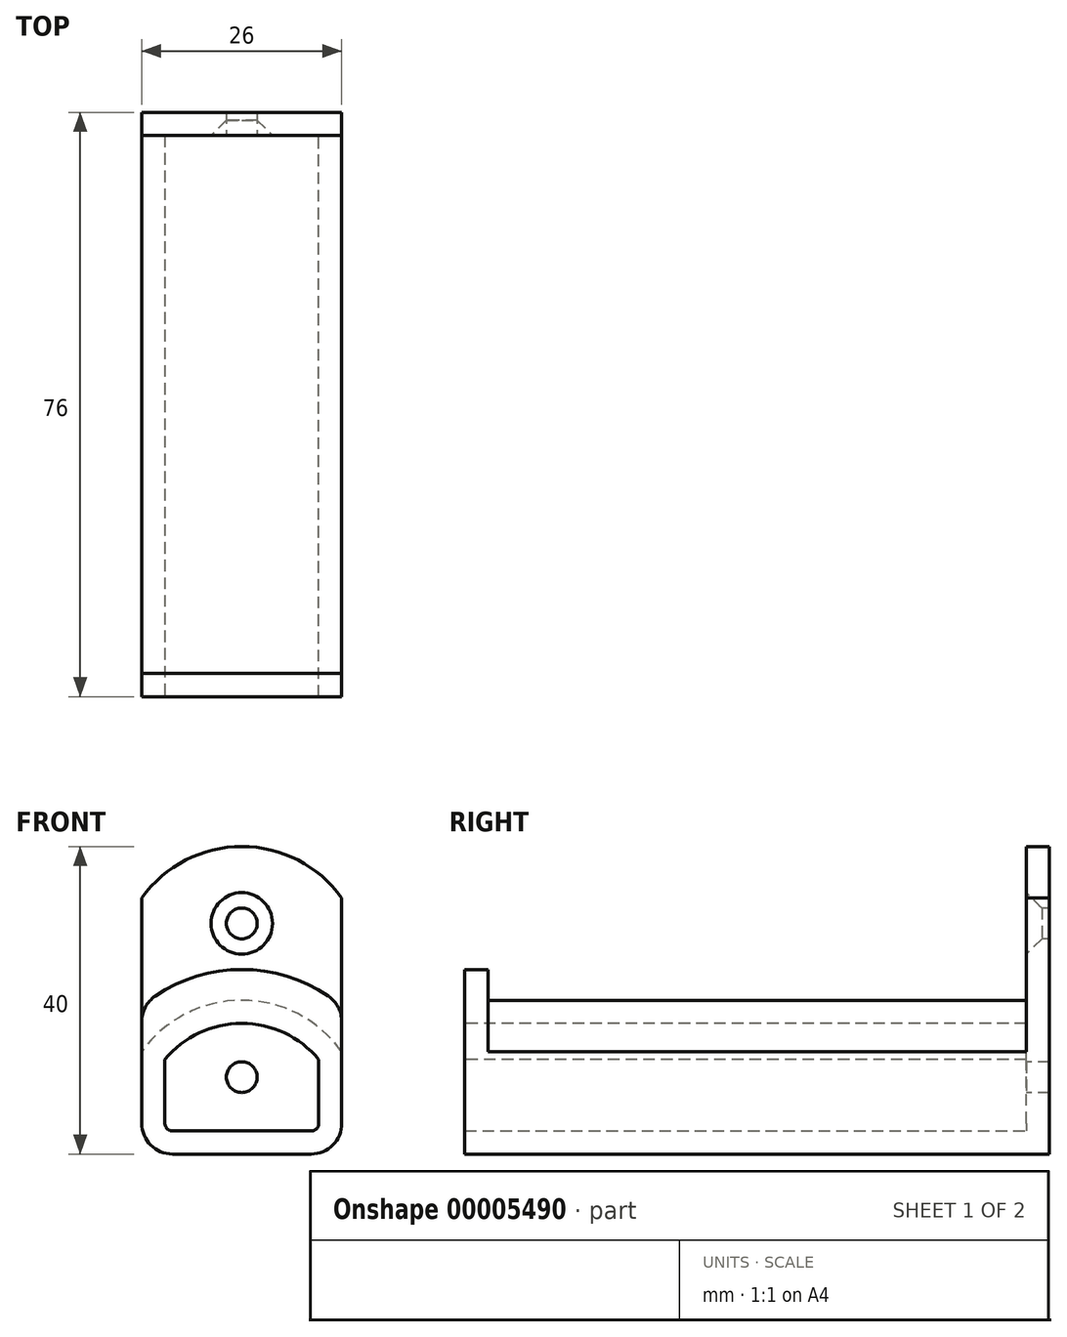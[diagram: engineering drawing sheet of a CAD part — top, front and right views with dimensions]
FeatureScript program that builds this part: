
annotation { "Feature Type Name" : "Feature", "Feature Type Description" : "" }
export const myFeature = defineFeature(function(context is Context, id is Id, definition is map)
    precondition{}
    {
        {
            var Q0;
            Q0=qCreatedBy(makeId("Front.planeOp"),FACE);
            var sketch = newSketch(context, id + "F0", { "sketchPlane" : qUnion([Q0])});
            skArc(sketch, "E0", {"start": v(13, 9.33) * mm, "mid": v(0, 16) * mm, "end": v(-13, 9.33) * mm});
            skLineSegment(sketch, "E1", {"start": v(-13, -4) * mm, "end": v(13, -4) * mm});
            skCircle(sketch, "E2", {"center": v(0, 5.33) * mm, "radius": 16 * mm, "construction": true});
            skLineSegment(sketch, "E3", {"start": v(-13, -4) * mm, "end": v(-13, 9.33) * mm});
            skLineSegment(sketch, "E4", {"start": v(13, -4) * mm, "end": v(13, 9.33) * mm});
            skLineSegment(sketch, "E5", {"start": v(0, 0) * mm, "end": v(0, 24.31) * mm, "construction": true});
            skLineSegment(sketch, "E6", {"start": v(-13, 9.33) * mm, "end": v(-13, 15.2) * mm});
            skLineSegment(sketch, "E7", {"start": v(13, 9.33) * mm, "end": v(13, 15.2) * mm});
            skArc(sketch, "E8.0", {"start": v(13, 15.2) * mm, "mid": v(0, 20) * mm, "end": v(-13, 15.2) * mm});
            skSolve(sketch);
        }
        {
            var Q0;
            Q0=makeQuery(id+"F0.imprint","IMPRINT",FACE,{"disambiguationData":[TD([[makeQuery(id+"F0.imprint","IMPRINT",EDGE,{"derivedFrom":sQuery(id+"F0.wireOp",EDGE,"E0")}),1.0]])]});
            extrude(context, id + "F1", {"entities" : qUnion([Q0]), "oppositeDirection" : true, "depth" : 70 * mm});
        }
        {
            var Q0;
            Q0=makeQuery(id+"F0.imprint","IMPRINT",FACE,{"disambiguationData":[TD([[makeQuery(id+"F0.imprint","IMPRINT",EDGE,{"derivedFrom":sQuery(id+"F0.wireOp",EDGE,"E0")}),1.0]])]});
            var Q1;
            Q1=makeQuery(id+"F0.imprint","IMPRINT",FACE,{"disambiguationData":[TD([[makeQuery(id+"F0.imprint","IMPRINT",EDGE,{"derivedFrom":sQuery(id+"F0.wireOp",EDGE,"E0")}),-1.0]])]});
            extrude(context, id + "F2", {"entities" : qUnion([Q0, Q1]), "operationType" : NewBodyOperationType.ADD, "depth" : 3 * mm});
        }
        {
            var Q0;
            {var subQ0=sQuery(id+"F0.wireOp",EDGE,"E1");var subQ1=sQuery(id+"F0.wireOp",EDGE,"E3");Q0=makeQuery(id+"F2.boolean.opBoolean","MERGE",EDGE,{"derivedFrom":[makeQuery(id+"F1.opExtrude","SWEPT_EDGE",EDGE,{"disambiguationData":[OSD([subQ0,subQ1])]}),makeQuery(id+"F2.opExtrude","SWEPT_EDGE",EDGE,{"disambiguationData":[OSD([subQ0,subQ1])]})]});}
            var Q1;
            {var subQ0=sQuery(id+"F0.wireOp",EDGE,"E1");var subQ1=sQuery(id+"F0.wireOp",EDGE,"E4");Q1=makeQuery(id+"F2.boolean.opBoolean","MERGE",EDGE,{"derivedFrom":[makeQuery(id+"F1.opExtrude","SWEPT_EDGE",EDGE,{"disambiguationData":[OSD([subQ0,subQ1])]}),makeQuery(id+"F2.opExtrude","SWEPT_EDGE",EDGE,{"disambiguationData":[OSD([subQ0,subQ1])]})]});}
            var Q2;
            Q2=makeQuery(id+"F2.opExtrude","SWEPT_EDGE",EDGE,{"disambiguationData":[OSD([sQuery(id+"F0.wireOp",EDGE,"E7"),sQuery(id+"F0.wireOp",EDGE,"E8.0")])]});
            var Q3;
            Q3=makeQuery(id+"F2.opExtrude","SWEPT_EDGE",EDGE,{"disambiguationData":[OSD([sQuery(id+"F0.wireOp",EDGE,"E6"),sQuery(id+"F0.wireOp",EDGE,"E8.0")])]});
            fillet(context, id + "F3", {"entities" : qUnion([Q0, Q1, Q2, Q3]), "radius" : 4 * mm, "tangentPropagation" : true, "allowEdgeOverflow" : false});
        }
        {
            var Q0;
            Q0=makeQuery(id+"F1.opExtrude","CAP_FACE",FACE,{"disambiguationData":[OSD([sQuery(id+"F0.wireOp",EDGE,"E0"),sQuery(id+"F0.wireOp",EDGE,"E1"),sQuery(id+"F0.wireOp",EDGE,"E3"),sQuery(id+"F0.wireOp",EDGE,"E4")])],"isStart":false});
            var sketch = newSketch(context, id + "F4", { "sketchPlane" : qUnion([Q0])});
            skArc(sketch, "E9.0", {"start": v(-13, 9.33) * mm, "mid": v(0, 16) * mm, "end": v(13, 9.33) * mm});
            skLineSegment(sketch, "E9.1", {"start": v(9, -4) * mm, "end": v(-9, -4) * mm});
            skLineSegment(sketch, "E10", {"start": v(0, -4) * mm, "end": v(0, 16) * mm, "construction": true});
            skCircle(sketch, "E11", {"center": v(0, 6) * mm, "radius": 2 * mm});
            skLineSegment(sketch, "E12", {"start": v(-13, 9.33) * mm, "end": v(-13, 29.33) * mm});
            skLineSegment(sketch, "E13", {"start": v(13, 9.33) * mm, "end": v(13, 29.33) * mm});
            skArc(sketch, "E14", {"start": v(13, 29.33) * mm, "mid": v(0, 36) * mm, "end": v(-13, 29.33) * mm});
            skCircle(sketch, "E15", {"center": v(0, 26) * mm, "radius": 2 * mm});
            skSolve(sketch);
        }
        {
            var Q0;
            Q0=makeQuery(id+"F4.imprint","IMPRINT",FACE,{"disambiguationData":[TD([[makeQuery(id+"F4.imprint","IMPRINT",EDGE,{"derivedFrom":sQuery(id+"F4.wireOp",EDGE,"E9.0")}),1.0]])]});
            var Q1;
            Q1=makeQuery(id+"F4.imprint","IMPRINT",FACE,{"disambiguationData":[TD([[makeQuery(id+"F4.imprint","IMPRINT",EDGE,{"derivedFrom":sQuery(id+"F4.wireOp",EDGE,"E9.0")}),-1.0]])]});
            var Q2;
            Q2=makeQuery(id+"F4.imprint","IMPRINT",FACE,{"disambiguationData":[TD([[makeQuery(id+"F4.imprint","IMPRINT",EDGE,{"derivedFrom":sQuery(id+"F4.wireOp",EDGE,"E11")}),1.0]])]});
            extrude(context, id + "F5", {"entities" : qUnion([Q0, Q1, Q2]), "operationType" : NewBodyOperationType.ADD, "depth" : 3 * mm});
        }
        {
            var Q0;
            Q0=makeQuery(id+"F2.opExtrude","CAP_FACE",FACE,{"disambiguationData":[OSD([sQuery(id+"F0.wireOp",EDGE,"E1"),sQuery(id+"F0.wireOp",EDGE,"E3"),sQuery(id+"F0.wireOp",EDGE,"E4"),sQuery(id+"F0.wireOp",EDGE,"E6"),sQuery(id+"F0.wireOp",EDGE,"E7"),sQuery(id+"F0.wireOp",EDGE,"E8.0")])],"isStart":false});
            shell(context, id + "F6", {"entities" : qUnion([Q0]), "thickness" : 3 * mm});
        }
        {
            var Q0;
            Q0=makeQuery(id+"F4.imprint","IMPRINT",FACE,{"disambiguationData":[TD([[makeQuery(id+"F4.imprint","IMPRINT",EDGE,{"derivedFrom":sQuery(id+"F4.wireOp",EDGE,"E11")}),1.0]])]});
            extrude(context, id + "F7", {"entities" : qUnion([Q0]), "operationType" : NewBodyOperationType.REMOVE, "depth" : 25 * mm});
        }
        {
            var Q0;
            Q0=makeQuery(id+"F5.opExtrude","CAP_EDGE",EDGE,{"disambiguationData":[OSD([sQuery(id+"F4.wireOp",EDGE,"E15")])],"isStart":true});
            var Q1;
            Q1=makeQuery(id+"F7.boolean.opBoolean","COPY",EDGE,{"derivedFrom":makeQuery(id+"F7.opExtrude","CAP_EDGE",EDGE,{"disambiguationData":[OSD([sQuery(id+"F4.wireOp",EDGE,"E11")])],"isStart":true})});
            chamfer(context, id + "F8", {"entities" : qUnion([Q0, Q1]), "width" : 2 * mm, "tangentPropagation" : true});
        }
    });
